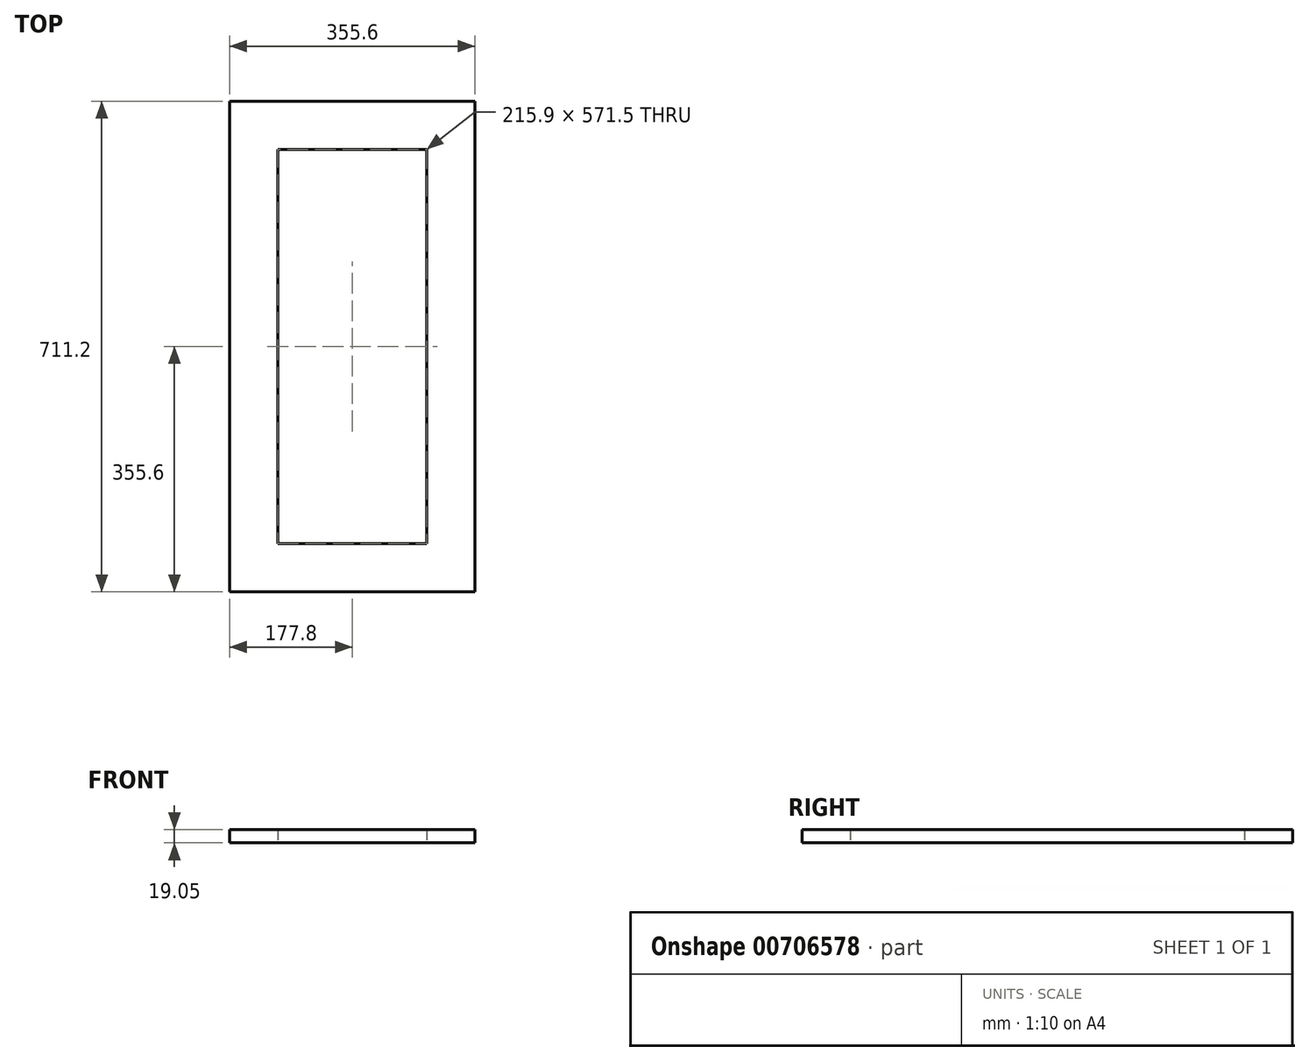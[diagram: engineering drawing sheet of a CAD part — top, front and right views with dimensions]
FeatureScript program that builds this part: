
annotation { "Feature Type Name" : "Feature", "Feature Type Description" : "" }
export const myFeature = defineFeature(function(context is Context, id is Id, definition is map)
    precondition{}
    {
        {
            var Q0;
            Q0=qCreatedBy(makeId("Top.planeOp"),FACE);
            var sketch = newSketch(context, id + "F0", { "sketchPlane" : qUnion([Q0])});
            skLineSegment(sketch, "E0.bottom", {"start": v(177.8, 355.6) * mm, "end": v(-177.8, 355.6) * mm});
            skLineSegment(sketch, "E0.top", {"start": v(177.8, -355.6) * mm, "end": v(-177.8, -355.6) * mm});
            skLineSegment(sketch, "E0.left", {"start": v(177.8, 355.6) * mm, "end": v(177.8, -355.6) * mm});
            skLineSegment(sketch, "E0.right", {"start": v(-177.8, 355.6) * mm, "end": v(-177.8, -355.6) * mm});
            skPoint(sketch, "E0.middle", {"position": v(0, 0) * mm});
            skLineSegment(sketch, "E1", {"start": v(-177.8, 355.6) * mm, "end": v(-107.95, 355.6) * mm});
            skLineSegment(sketch, "E2", {"start": v(-107.95, 355.6) * mm, "end": v(-107.95, 285.75) * mm});
            skLineSegment(sketch, "E3", {"start": v(177.8, -355.6) * mm, "end": v(107.95, -355.6) * mm});
            skLineSegment(sketch, "E4", {"start": v(107.95, -355.6) * mm, "end": v(107.95, -285.75) * mm});
            skLineSegment(sketch, "E5.bottom", {"start": v(-107.95, 285.75) * mm, "end": v(107.95, 285.75) * mm});
            skLineSegment(sketch, "E5.top", {"start": v(-107.95, -285.75) * mm, "end": v(107.95, -285.75) * mm});
            skLineSegment(sketch, "E5.left", {"start": v(-107.95, 285.75) * mm, "end": v(-107.95, -285.75) * mm});
            skLineSegment(sketch, "E5.right", {"start": v(107.95, 285.75) * mm, "end": v(107.95, -285.75) * mm});
            skSolve(sketch);
        }
        {
            var Q0;
            Q0=makeQuery(id+"F0.imprint","IMPRINT",FACE,{"disambiguationData":[TD([[makeQuery(id+"F0.imprint","IMPRINT",EDGE,{"derivedFrom":sQuery(id+"F0.wireOp",EDGE,"E0.top")}),-1.0]])]});
            var Q1;
            Q1=makeQuery(id+"F0.imprint","IMPRINT",FACE,{"disambiguationData":[TD([[makeQuery(id+"F0.imprint","IMPRINT",EDGE,{"derivedFrom":sQuery(id+"F0.wireOp",EDGE,"E0.bottom")}),1.0]])]});
            extrude(context, id + "F1", {"entities" : qUnion([Q0, Q1]), "depth" : 19.05 * mm, "offsetDistance" : 25.4 * mm});
        }
    });
